# Revit family: Sideboard-Teknion-CFFQL-Figure_36H_Quad_Accomodation_FP_Cool_drawer_Low_Base-R2023
name_source: partatom
category: Furniture
units: mm (PartAtom-declared; Revit-internal decimal feet)

## family parameters
Always vertical = Yes
Cut with Voids When Loaded = No
Enable Cutting in Views = No
OmniClass Number = 23.40.20.00
OmniClass Title = General Furniture and Specialties
Render Appearance Source = Family Geometry
Room Calculation Point = No
Shared = Yes
Work Plane-Based = Yes

## types (1)
- (HWFH) H.Door/ Waste/ Cutouts for Fridge Fridge/ H.Door
    AV Cutout = Yes
    Assembly Code = E2020200
    Default Elevation = 48 "
    Depth = 26 "
    Description = 36H Quad Sideboard, Accomodation for F&P Cool Drawer, Low Base
    Dim1 = 15 "
    H Door = 17.306 "
    HWFH = Yes
    Height = 37 "
    Manufacturer = Teknion
    Manufacturer Fax = 416.661.4586
    Model = CFFQL_HWFH
    Part Number = CFFQL
    Product Documentation Link = https://d2r72yk5wmppdj.cloudfront.net
    Product Line = Custom Wood
    Product Page URL = https://www.teknion.com
    Series = Figure
    Sustainability Data = https://www.teknion.com
    URL = www.teknion.com
    Unit Weight URL = http://www.teknion.com
    Warranty = http://www.teknion.com
    Width = 108 "

## geometry (parser evidence)
native form markers: Sweep x6
no freeform markers — native parametric forms only
